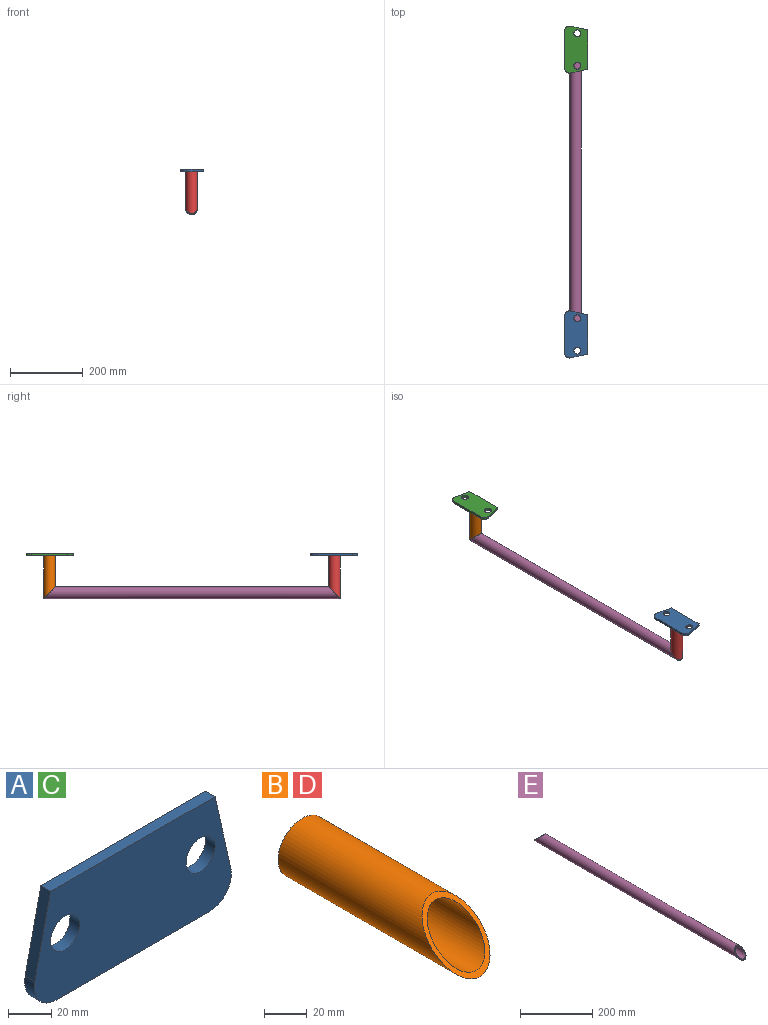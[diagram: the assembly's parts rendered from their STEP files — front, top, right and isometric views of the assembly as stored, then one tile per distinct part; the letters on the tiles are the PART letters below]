
ASSEMBLY  parts=5 mates=4
PART A: 10 faces, bbox 129.3x6.4x63.5 mm
  f0: plane 107.95x6.35mm, normal (0,0,1), area 685.5mm2, adj f1,f7,f8,f9
  f1: plane 46x10.35mm, normal (-0.98,0,0.22), area 299.4mm2, adj f0,f2,f8,f9
  f2: cylinder r=14.35mm len=17.5mm, axis (0,1,0), area 163.3mm2, adj f1,f3,f8,f9
  f3: plane 100.65x6.35mm, normal (0,0,-1), area 639.1mm2, adj f2,f4,f8,f9
  f4: cylinder r=14.35mm len=17.5mm, axis (0,1,0), area 163.3mm2, adj f3,f7,f8,f9
  f5: cylinder r=9.53mm len=19.05mm, axis (0,1,0), area 380mm2, adj f8,f9
  f6: cylinder r=9.53mm len=19.05mm, axis (0,1,0), area 380mm2, adj f8,f9
  f7: plane 46x10.35mm, normal (0.98,0,0.22), area 299.4mm2, adj f0,f4,f8,f9
  f8: plane 129.35x63.5mm, normal (0,-1,0), area 7046.2mm2, adj f0,f1,f2,f3,f4,f5,f6,f7
  f9: plane 129.35x63.5mm, normal (0,1,0), area 7046.2mm2, adj f0,f1,f2,f3,f4,f5,f6,f7
PART B: 4 faces, bbox 31.8x117.7x31.8 mm
  f0: cylinder r=13.46mm len=115.25mm, axis (0,1,0), area 8593.7mm2, adj f2,f3
  f1: cylinder r=15.88mm len=117.69mm, axis (0,1,0), area 10134.1mm2, adj f2,f3
  f2: plane 31.75x31.75mm, normal (0,1,0), area 222.4mm2, adj f0,f1
  f3: plane 31.75x31.75mm, normal (0,-0.71,0.71), area 314.5mm2, adj f0,f1
PART C: same geometry as A
PART D: same geometry as B
PART E: 4 faces, bbox 38.4x821.3x38.4 mm
  f0: cylinder r=13.46mm len=809.75mm, axis (0,1,0), area 66198.8mm2, adj f2,f3
  f1: cylinder r=15.88mm len=814.6mm, axis (0,1,0), area 78064.6mm2, adj f2,f3
  f2: plane 38.43x38.43mm, normal (0,0.71,0.71), area 314.5mm2, adj f0,f1
  f3: plane 31.75x31.75mm, normal (0,-0.71,0.71), area 314.5mm2, adj f0,f1
PLACE A rot(axis=(0.58,0.58,0.58),120deg) t=(-226.66,-544.81,-53.65)mm
PLACE B rot(axis=(1,0,0),90deg) t=(-227.73,237.83,-60)mm
PLACE C rot(axis=(0.58,0.58,0.58),120deg) t=(-226.66,237.83,-53.65)mm
PLACE D rot(axis=(0,-0.71,-0.71),180deg) t=(-227.73,-544.81,-60)mm
PLACE E t=(-227.73,253.7,-161.6)mm
MATE parallel D.f3 <-> E.f3  axis (0,0.71,-0.71) through (-227.73,-544.81,-161.6)mm
MATE parallel D.f3 <-> E.f3  axis (0,0.71,-0.71) through (-227.73,-544.81,-161.6)mm
MATE parallel C.f8 <-> B.f1  axis (0,0,-1) through (-227.73,237.83,-60)mm
MATE parallel A.f8 <-> D.f0  axis (0,0,1) through (-227.73,-544.81,-60)mm
